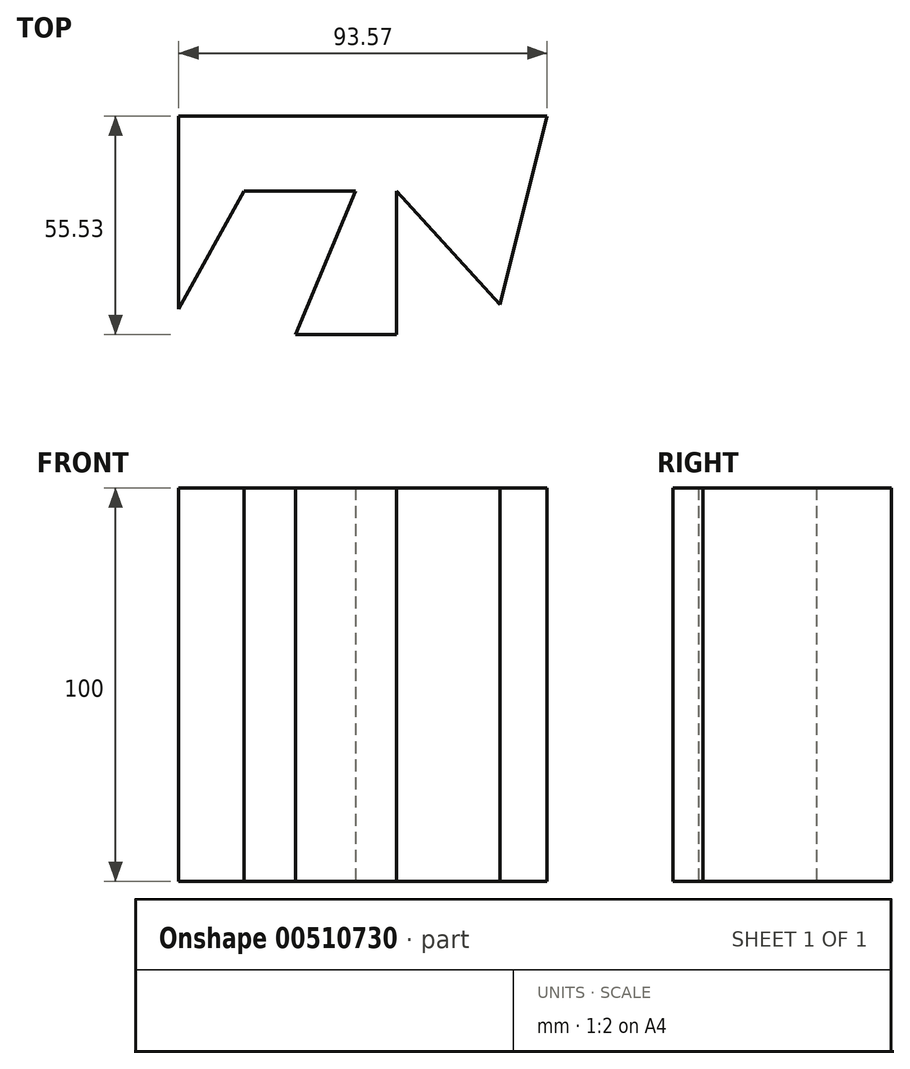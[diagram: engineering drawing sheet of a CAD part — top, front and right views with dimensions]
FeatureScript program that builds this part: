
annotation { "Feature Type Name" : "Feature", "Feature Type Description" : "" }
export const myFeature = defineFeature(function(context is Context, id is Id, definition is map)
    precondition{}
    {
        {
            var Q0;
            Q0=qCreatedBy(makeId("Top.planeOp"),FACE);
            var sketch = newSketch(context, id + "F0", { "sketchPlane" : qUnion([Q0])});
            skLineSegment(sketch, "E0", {"start": v(-45.47, 0) * mm, "end": v(48.68, 0) * mm});
            skLineSegment(sketch, "E1", {"start": v(48.68, 0) * mm, "end": v(36.73, -47.95) * mm});
            skLineSegment(sketch, "E2", {"start": v(36.73, -47.95) * mm, "end": v(10.5, -19.1) * mm});
            skLineSegment(sketch, "E3", {"start": v(10.5, -19.1) * mm, "end": v(10.5, -55.53) * mm});
            skLineSegment(sketch, "E4", {"start": v(10.5, -55.53) * mm, "end": v(-15.16, -55.53) * mm});
            skLineSegment(sketch, "E5", {"start": v(-15.16, -55.53) * mm, "end": v(0, -19.1) * mm});
            skLineSegment(sketch, "E6", {"start": v(0, -19.1) * mm, "end": v(-28.27, -19.1) * mm});
            skLineSegment(sketch, "E7", {"start": v(-28.27, -19.1) * mm, "end": v(-44.89, -49.11) * mm});
            skLineSegment(sketch, "E8", {"start": v(-44.89, -49.11) * mm, "end": v(-44.89, 0) * mm});
            skSolve(sketch);
        }
        {
            var Q0;
            {var subQ0=sQuery(id+"F0.wireOp",EDGE,"E1");Q0=makeQuery(id+"F0.imprint","IMPRINT",FACE,{"disambiguationData":[TD([[makeQuery(id+"F0.imprint","IMPRINT",EDGE,{"derivedFrom":subQ0}),-1.0]])]});}
            extrude(context, id + "F1", {"entities" : qUnion([Q0]), "endBound" : BoundingType.SYMMETRIC, "depth" : 100 * mm});
        }
    });
